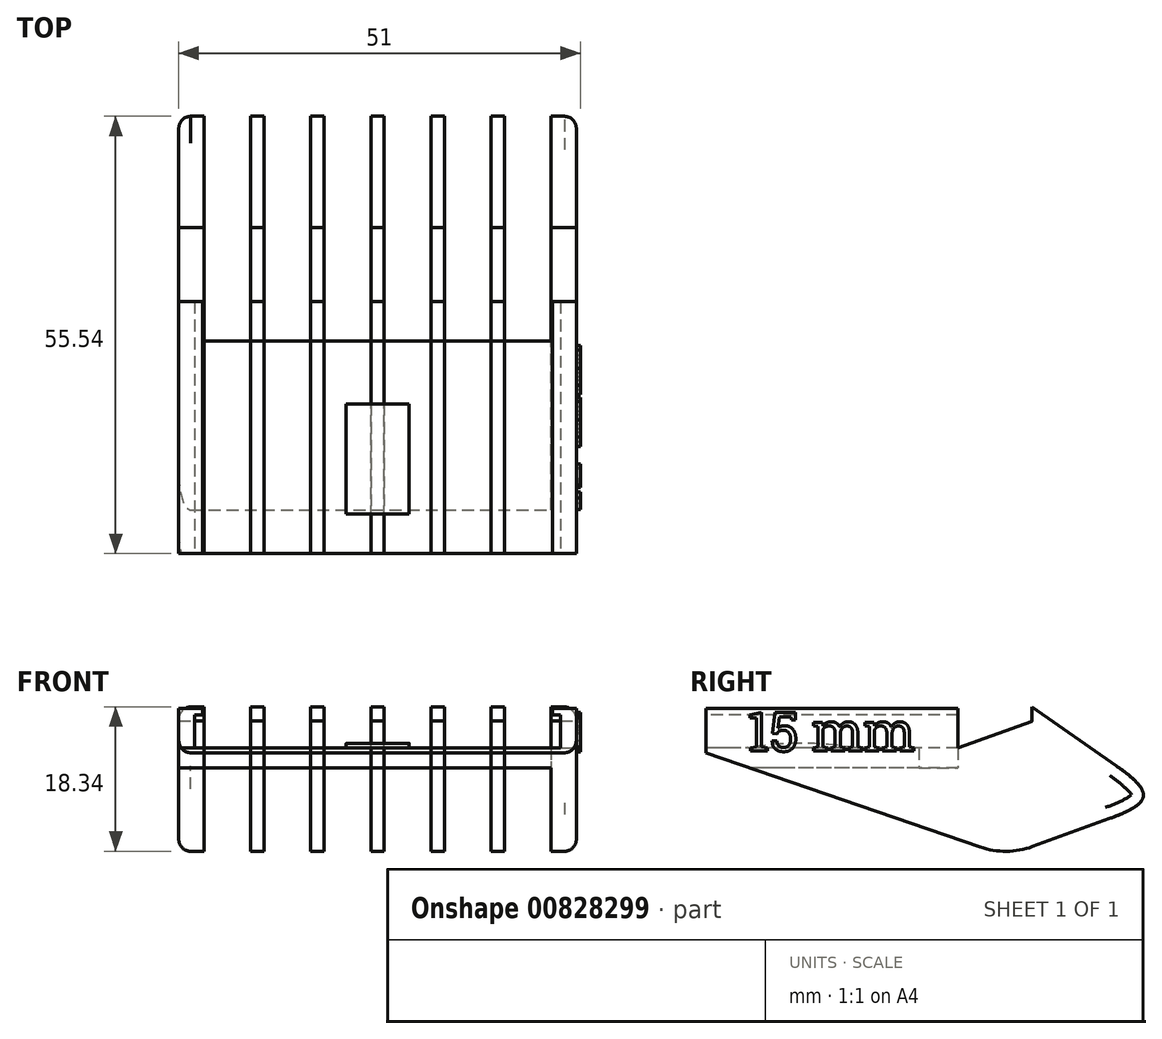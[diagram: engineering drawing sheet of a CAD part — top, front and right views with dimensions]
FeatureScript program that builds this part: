
annotation { "Feature Type Name" : "Feature", "Feature Type Description" : "" }
export const myFeature = defineFeature(function(context is Context, id is Id, definition is map)
    precondition{}
    {
        {
            var Q0;
            Q0=qCreatedBy(makeId("Top.planeOp"),FACE);
            var sketch = newSketch(context, id + "F0", { "sketchPlane" : qUnion([Q0])});
            skLineSegment(sketch, "E0.top", {"start": v(25.25, -16) * mm, "end": v(-25.25, -16) * mm});
            skLineSegment(sketch, "E0.left", {"start": v(25.25, 16) * mm, "end": v(25.25, -16) * mm});
            skLineSegment(sketch, "E0.right", {"start": v(-25.25, 16) * mm, "end": v(-25.25, -16) * mm});
            skPoint(sketch, "E0.middle", {"position": v(0, 0) * mm});
            skLineSegment(sketch, "E1", {"start": v(-22.05, 11) * mm, "end": v(22.05, 11) * mm});
            skLineSegment(sketch, "E2", {"start": v(22.05, 11) * mm, "end": v(22.05, 16) * mm});
            skLineSegment(sketch, "E3", {"start": v(22.05, 16) * mm, "end": v(25.25, 16) * mm});
            skLineSegment(sketch, "E4", {"start": v(-22.05, 11) * mm, "end": v(-22.05, 16) * mm});
            skLineSegment(sketch, "E5", {"start": v(-22.05, 16) * mm, "end": v(-25.25, 16) * mm});
            skSolve(sketch);
        }
        {
            var Q0;
            Q0=qSketchRegion(id+"F0",true);
            extrude(context, id + "F1", {"entities" : qUnion([Q0]), "depth" : 2.5 * mm, "offsetDistance" : 25 * mm});
        }
        {
            var Q0;
            Q0=makeQuery(id+"F1.opExtrude","SWEPT_FACE",FACE,{"disambiguationData":[OSD([sQuery(id+"F0.wireOp",EDGE,"E0.top")])]});
            var sketch = newSketch(context, id + "F2", { "sketchPlane" : qUnion([Q0])});
            skLineSegment(sketch, "E6.0", {"start": v(25.25, 2.5) * mm, "end": v(-25.25, 2.5) * mm});
            skLineSegment(sketch, "E7", {"start": v(25.25, 2.5) * mm, "end": v(25.25, 7.5) * mm});
            skLineSegment(sketch, "E8", {"start": v(25.25, 7.5) * mm, "end": v(22.25, 7.5) * mm});
            skLineSegment(sketch, "E9", {"start": v(22.25, 7.5) * mm, "end": v(22.25, 6.7) * mm});
            skLineSegment(sketch, "E10", {"start": v(22.25, 6.7) * mm, "end": v(23.25, 6.7) * mm});
            skLineSegment(sketch, "E11", {"start": v(23.25, 6.7) * mm, "end": v(23.25, 2.5) * mm});
            skLineSegment(sketch, "E12", {"start": v(23.25, 2.5) * mm, "end": v(25.25, 2.5) * mm});
            skLineSegment(sketch, "E13.MirrorCS", {"start": v(-25.25, 2.5) * mm, "end": v(-25.25, 7.5) * mm});
            skLineSegment(sketch, "E14.MirrorCS", {"start": v(-25.25, 7.5) * mm, "end": v(-22.25, 7.5) * mm});
            skLineSegment(sketch, "E15.MirrorCS", {"start": v(-22.25, 7.5) * mm, "end": v(-22.25, 6.7) * mm});
            skLineSegment(sketch, "E16.MirrorCS", {"start": v(-22.25, 6.7) * mm, "end": v(-23.25, 6.7) * mm});
            skLineSegment(sketch, "E17.MirrorCS", {"start": v(-23.25, 6.7) * mm, "end": v(-23.25, 2.5) * mm});
            skSolve(sketch);
        }
        {
            var Q0;
            Q0=qSketchRegion(id+"F2",true);
            var Q1;
            Q1=makeQuery(id+"F1.opExtrude","SWEPT_FACE",FACE,{"disambiguationData":[OSD([sQuery(id+"F0.wireOp",EDGE,"E3")])]});
            extrude(context, id + "F3", {"entities" : qUnion([Q0]), "operationType" : NewBodyOperationType.ADD, "endBound" : BoundingType.UP_TO_SURFACE, "oppositeDirection" : true, "depth" : 25 * mm, "endBoundEntityFace" : qUnion([Q1]), "offsetDistance" : 25 * mm});
        }
        {
            var Q0;
            Q0=makeQuery(id+"F3.boolean.opBoolean","MERGE",FACE,{"derivedFrom":[makeQuery(id+"F1.opExtrude","SWEPT_FACE",FACE,{"disambiguationData":[OSD([sQuery(id+"F0.wireOp",EDGE,"E0.left")])]}),makeQuery(id+"F3.opExtrude","SWEPT_FACE",FACE,{"disambiguationData":[OSD([sQuery(id+"F2.wireOp",EDGE,"E7")])]})]});
            var sketch = newSketch(context, id + "F4", { "sketchPlane" : qUnion([Q0])});
            skLineSegment(sketch, "E18.0", {"start": v(16, 2.5) * mm, "end": v(-16, 2.5) * mm});
            skLineSegment(sketch, "E19.0", {"start": v(11, 2.5) * mm, "end": v(11, 0) * mm});
            skLineSegment(sketch, "E20.0", {"start": v(16, 2.5) * mm, "end": v(16, 0) * mm});
            skLineSegment(sketch, "E21", {"start": v(11, 0) * mm, "end": v(11, 2.5) * mm});
            skLineSegment(sketch, "E22", {"start": v(11, 2.5) * mm, "end": v(16, 2.5) * mm});
            skLineSegment(sketch, "E23", {"start": v(16, 2.5) * mm, "end": v(25.4, 5.92) * mm});
            skLineSegment(sketch, "E24", {"start": v(25.4, 5.92) * mm, "end": v(25.4, 7.72) * mm});
            skLineSegment(sketch, "E25", {"start": v(25.4, 7.72) * mm, "end": v(42.09, -3.97) * mm});
            skLineSegment(sketch, "E26", {"start": v(42.09, -3.97) * mm, "end": v(25.46, -10.02) * mm});
            skArc(sketch, "E27", {"start": v(18.79, -10.08) * mm, "mid": v(22.13, -10.62) * mm, "end": v(25.46, -10.02) * mm});
            skLineSegment(sketch, "E28", {"start": v(-16, 1.9) * mm, "end": v(18.79, -10.08) * mm});
            skLineSegment(sketch, "E29", {"start": v(-16, 2.5) * mm, "end": v(-16, 1.9) * mm});
            skSolve(sketch);
        }
        {
            var Q0;
            Q0=qSketchRegion(id+"F4",true);
            var Q1;
            Q1=makeQuery(id+"F3.boolean.opBoolean","MERGE",FACE,{"derivedFrom":[makeQuery(id+"F1.opExtrude","SWEPT_FACE",FACE,{"disambiguationData":[OSD([sQuery(id+"F0.wireOp",EDGE,"E0.right")])]}),makeQuery(id+"F3.opExtrude","SWEPT_FACE",FACE,{"disambiguationData":[OSD([sQuery(id+"F2.wireOp",EDGE,"E13.MirrorCS")])]})]});
            extrude(context, id + "F5", {"entities" : qUnion([Q0]), "operationType" : NewBodyOperationType.ADD, "endBound" : BoundingType.UP_TO_SURFACE, "oppositeDirection" : true, "depth" : 25 * mm, "endBoundEntityFace" : qUnion([Q1]), "offsetDistance" : 25 * mm});
        }
        {
            var Q0;
            Q0=makeQuery(id+"F5.opExtrude","SWEPT_FACE",FACE,{"disambiguationData":[OSD([sQuery(id+"F4.wireOp",EDGE,"E26")])]});
            var sketch = newSketch(context, id + "F6", { "sketchPlane" : qUnion([Q0])});
            skLineSegment(sketch, "E30.bottom", {"start": v(22.05, -38.2) * mm, "end": v(16.12, -38.2) * mm});
            skLineSegment(sketch, "E30.top", {"start": v(22.05, 31.14) * mm, "end": v(16.12, 31.14) * mm});
            skLineSegment(sketch, "E30.left", {"start": v(22.05, -38.2) * mm, "end": v(22.05, 31.14) * mm});
            skLineSegment(sketch, "E30.right", {"start": v(16.12, -38.2) * mm, "end": v(16.12, 31.14) * mm});
            skLineSegment(sketch, "E31.1.0.0", {"start": v(14.42, -38.2) * mm, "end": v(14.42, 31.14) * mm});
            skLineSegment(sketch, "E31.1.0.1", {"start": v(8.48, -38.2) * mm, "end": v(8.48, 31.14) * mm});
            skLineSegment(sketch, "E31.1.0.2", {"start": v(14.42, 31.14) * mm, "end": v(8.48, 31.14) * mm});
            skLineSegment(sketch, "E31.1.0.3", {"start": v(14.42, -38.2) * mm, "end": v(8.48, -38.2) * mm});
            skLineSegment(sketch, "E31.2.0.0", {"start": v(6.78, -38.2) * mm, "end": v(6.78, 31.14) * mm});
            skLineSegment(sketch, "E31.2.0.1", {"start": v(0.85, -38.2) * mm, "end": v(0.85, 31.14) * mm});
            skLineSegment(sketch, "E31.2.0.2", {"start": v(6.78, 31.14) * mm, "end": v(0.85, 31.14) * mm});
            skLineSegment(sketch, "E31.2.0.3", {"start": v(6.78, -38.2) * mm, "end": v(0.85, -38.2) * mm});
            skLineSegment(sketch, "E31.3.0.0", {"start": v(-0.85, -38.2) * mm, "end": v(-0.85, 31.14) * mm});
            skLineSegment(sketch, "E31.3.0.1", {"start": v(-6.78, -38.2) * mm, "end": v(-6.78, 31.14) * mm});
            skLineSegment(sketch, "E31.3.0.2", {"start": v(-0.85, 31.14) * mm, "end": v(-6.78, 31.14) * mm});
            skLineSegment(sketch, "E31.3.0.3", {"start": v(-0.85, -38.2) * mm, "end": v(-6.78, -38.2) * mm});
            skLineSegment(sketch, "E31.4.0.0", {"start": v(-8.48, -38.2) * mm, "end": v(-8.48, 31.14) * mm});
            skLineSegment(sketch, "E31.4.0.1", {"start": v(-14.42, -38.2) * mm, "end": v(-14.42, 31.14) * mm});
            skLineSegment(sketch, "E31.4.0.2", {"start": v(-8.48, 31.14) * mm, "end": v(-14.42, 31.14) * mm});
            skLineSegment(sketch, "E31.4.0.3", {"start": v(-8.48, -38.2) * mm, "end": v(-14.42, -38.2) * mm});
            skLineSegment(sketch, "E31.5.0.0", {"start": v(-16.12, -38.2) * mm, "end": v(-16.12, 31.14) * mm});
            skLineSegment(sketch, "E31.5.0.1", {"start": v(-22.05, -38.2) * mm, "end": v(-22.05, 31.14) * mm});
            skLineSegment(sketch, "E31.5.0.2", {"start": v(-16.12, 31.14) * mm, "end": v(-22.05, 31.14) * mm});
            skLineSegment(sketch, "E31.5.0.3", {"start": v(-16.12, -38.2) * mm, "end": v(-22.05, -38.2) * mm});
            skLineSegment(sketch, "E31.direction1", {"start": v(22.05, -38.2) * mm, "end": v(14.42, -38.2) * mm, "construction": true});
            skSolve(sketch);
        }
        {
            var Q0;
            Q0=qSketchRegion(id+"F6",true);
            extrude(context, id + "F7", {"entities" : qUnion([Q0]), "operationType" : NewBodyOperationType.REMOVE, "endBound" : BoundingType.UP_TO_NEXT, "oppositeDirection" : true, "depth" : 25 * mm, "offsetDistance" : 25 * mm});
        }
        {
            var Q0;
            Q0=qSketchRegion(id+"F0",true);
            extrude(context, id + "F8", {"entities" : qUnion([Q0]), "depth" : 2.5 * mm, "offsetDistance" : 25 * mm});
        }
        {
            var Q0;
            Q0=qCreatedBy(makeId("Right.planeOp"),FACE);
            var sketch = newSketch(context, id + "F9", { "sketchPlane" : qUnion([Q0])});
            skLineSegment(sketch, "E32.0", {"start": v(16, 2.5) * mm, "end": v(-16, 2.5) * mm});
            skLineSegment(sketch, "E33.0", {"start": v(11, 2.5) * mm, "end": v(11, 0) * mm});
            skArc(sketch, "E34", {"start": v(3, 2.5) * mm, "mid": v(-4, 3.1) * mm, "end": v(-11, 2.5) * mm});
            skSolve(sketch);
        }
        {
            var Q0;
            Q0=qSketchRegion(id+"F9",true);
            extrude(context, id + "F10", {"entities" : qUnion([Q0]), "endBound" : BoundingType.SYMMETRIC, "depth" : 8 * mm, "offsetDistance" : 25 * mm});
        }
        {
            var Q0;
            {var subQ0=sQuery(id+"F4.wireOp",EDGE,"E25");var subQ1=sQuery(id+"F4.wireOp",EDGE,"E26");Q0=makeQuery(id+"F7.boolean.opBoolean","SPLIT",EDGE,{"disambiguationData":[TD([makeQuery(id+"F1.opExtrude","SWEPT_FACE",FACE,{"disambiguationData":[OSD([sQuery(id+"F0.wireOp",EDGE,"E0.right")])]})])],"derivedFrom":makeQuery(id+"F5.opExtrude","SWEPT_EDGE",EDGE,{"disambiguationData":[OSD([subQ0,subQ1])]})});}
            var Q1;
            {var subQ0=sQuery(id+"F4.wireOp",EDGE,"E25");var subQ1=sQuery(id+"F4.wireOp",EDGE,"E26");Q1=makeQuery(id+"F7.boolean.opBoolean","SPLIT",EDGE,{"disambiguationData":[TD([makeQuery(id+"F7.opExtrude","SWEPT_FACE",FACE,{"disambiguationData":[OSD([sQuery(id+"F6.wireOp",EDGE,"E31.8.0.1")])]})])],"derivedFrom":makeQuery(id+"F5.opExtrude","SWEPT_EDGE",EDGE,{"disambiguationData":[OSD([subQ0,subQ1])]})});}
            var Q2;
            {var subQ0=sQuery(id+"F4.wireOp",EDGE,"E25");var subQ1=sQuery(id+"F4.wireOp",EDGE,"E26");Q2=makeQuery(id+"F7.boolean.opBoolean","SPLIT",EDGE,{"disambiguationData":[TD([makeQuery(id+"F7.opExtrude","SWEPT_FACE",FACE,{"disambiguationData":[OSD([sQuery(id+"F6.wireOp",EDGE,"E31.7.0.1")])]})])],"derivedFrom":makeQuery(id+"F5.opExtrude","SWEPT_EDGE",EDGE,{"disambiguationData":[OSD([subQ0,subQ1])]})});}
            var Q3;
            {var subQ0=sQuery(id+"F4.wireOp",EDGE,"E25");var subQ1=sQuery(id+"F4.wireOp",EDGE,"E26");Q3=makeQuery(id+"F7.boolean.opBoolean","SPLIT",EDGE,{"disambiguationData":[TD([makeQuery(id+"F7.opExtrude","SWEPT_FACE",FACE,{"disambiguationData":[OSD([sQuery(id+"F6.wireOp",EDGE,"E31.6.0.1")])]})])],"derivedFrom":makeQuery(id+"F5.opExtrude","SWEPT_EDGE",EDGE,{"disambiguationData":[OSD([subQ0,subQ1])]})});}
            var Q4;
            {var subQ0=sQuery(id+"F4.wireOp",EDGE,"E25");var subQ1=sQuery(id+"F4.wireOp",EDGE,"E26");Q4=makeQuery(id+"F7.boolean.opBoolean","SPLIT",EDGE,{"disambiguationData":[TD([makeQuery(id+"F1.opExtrude","SWEPT_FACE",FACE,{"disambiguationData":[OSD([sQuery(id+"F0.wireOp",EDGE,"E0.right")])]})])],"derivedFrom":makeQuery(id+"F5.opExtrude","SWEPT_EDGE",EDGE,{"disambiguationData":[OSD([subQ0,subQ1])]})});}
            var Q5;
            {var subQ0=sQuery(id+"F4.wireOp",EDGE,"E25");var subQ1=sQuery(id+"F4.wireOp",EDGE,"E26");Q5=makeQuery(id+"F7.boolean.opBoolean","SPLIT",EDGE,{"disambiguationData":[TD([makeQuery(id+"F7.opExtrude","SWEPT_FACE",FACE,{"disambiguationData":[OSD([sQuery(id+"F6.wireOp",EDGE,"E31.4.0.1")])]})])],"derivedFrom":makeQuery(id+"F5.opExtrude","SWEPT_EDGE",EDGE,{"disambiguationData":[OSD([subQ0,subQ1])]})});}
            var Q6;
            {var subQ0=sQuery(id+"F4.wireOp",EDGE,"E25");var subQ1=sQuery(id+"F4.wireOp",EDGE,"E26");Q6=makeQuery(id+"F7.boolean.opBoolean","SPLIT",EDGE,{"disambiguationData":[TD([makeQuery(id+"F7.opExtrude","SWEPT_FACE",FACE,{"disambiguationData":[OSD([sQuery(id+"F6.wireOp",EDGE,"E31.3.0.1")])]})])],"derivedFrom":makeQuery(id+"F5.opExtrude","SWEPT_EDGE",EDGE,{"disambiguationData":[OSD([subQ0,subQ1])]})});}
            var Q7;
            {var subQ0=sQuery(id+"F4.wireOp",EDGE,"E25");var subQ1=sQuery(id+"F4.wireOp",EDGE,"E26");Q7=makeQuery(id+"F7.boolean.opBoolean","SPLIT",EDGE,{"disambiguationData":[TD([makeQuery(id+"F7.opExtrude","SWEPT_FACE",FACE,{"disambiguationData":[OSD([sQuery(id+"F6.wireOp",EDGE,"E31.2.0.1")])]})])],"derivedFrom":makeQuery(id+"F5.opExtrude","SWEPT_EDGE",EDGE,{"disambiguationData":[OSD([subQ0,subQ1])]})});}
            var Q8;
            {var subQ0=sQuery(id+"F4.wireOp",EDGE,"E25");var subQ1=sQuery(id+"F4.wireOp",EDGE,"E26");Q8=makeQuery(id+"F7.boolean.opBoolean","SPLIT",EDGE,{"disambiguationData":[TD([makeQuery(id+"F7.opExtrude","SWEPT_FACE",FACE,{"disambiguationData":[OSD([sQuery(id+"F6.wireOp",EDGE,"E31.1.0.1")])]})])],"derivedFrom":makeQuery(id+"F5.opExtrude","SWEPT_EDGE",EDGE,{"disambiguationData":[OSD([subQ0,subQ1])]})});}
            var Q9;
            {var subQ0=sQuery(id+"F4.wireOp",EDGE,"E25");var subQ1=sQuery(id+"F4.wireOp",EDGE,"E26");Q9=makeQuery(id+"F7.boolean.opBoolean","SPLIT",EDGE,{"disambiguationData":[TD([makeQuery(id+"F7.opExtrude","SWEPT_FACE",FACE,{"disambiguationData":[OSD([sQuery(id+"F6.wireOp",EDGE,"E30.right")])]})])],"derivedFrom":makeQuery(id+"F5.opExtrude","SWEPT_EDGE",EDGE,{"disambiguationData":[OSD([subQ0,subQ1])]})});}
            var Q10;
            {var subQ0=sQuery(id+"F4.wireOp",EDGE,"E25");var subQ1=sQuery(id+"F4.wireOp",EDGE,"E26");Q10=makeQuery(id+"F7.boolean.opBoolean","SPLIT",EDGE,{"disambiguationData":[TD([makeQuery(id+"F1.opExtrude","SWEPT_FACE",FACE,{"disambiguationData":[OSD([sQuery(id+"F0.wireOp",EDGE,"E0.left")])]})])],"derivedFrom":makeQuery(id+"F5.opExtrude","SWEPT_EDGE",EDGE,{"disambiguationData":[OSD([subQ0,subQ1])]})});}
            fillet(context, id + "F11", {"entities" : qUnion([Q0, Q1, Q2, Q3, Q4, Q5, Q6, Q7, Q8, Q9, Q10]), "radius" : 3.8 * mm, "tangentPropagation" : true, "rho" : 0.6, "crossSection" : FilletCrossSection.CONIC, "allowEdgeOverflow" : false});
        }
        {
            var Q0;
            Q0=makeQuery(id+"F5.boolean.opBoolean","MERGE",FACE,{"derivedFrom":[makeQuery(id+"F3.boolean.opBoolean","MERGE",FACE,{"derivedFrom":[makeQuery(id+"F1.opExtrude","SWEPT_FACE",FACE,{"disambiguationData":[OSD([sQuery(id+"F0.wireOp",EDGE,"E0.left")])]}),makeQuery(id+"F3.opExtrude","SWEPT_FACE",FACE,{"disambiguationData":[OSD([sQuery(id+"F2.wireOp",EDGE,"E7")])]})]}),makeQuery(id+"F5.opExtrude","CAP_FACE",FACE,{"disambiguationData":[OSD([sQuery(id+"F4.wireOp",EDGE,"E18.0"),sQuery(id+"F4.wireOp",EDGE,"E22"),sQuery(id+"F4.wireOp",EDGE,"E23"),sQuery(id+"F4.wireOp",EDGE,"E24"),sQuery(id+"F4.wireOp",EDGE,"E25"),sQuery(id+"F4.wireOp",EDGE,"E26"),sQuery(id+"F4.wireOp",EDGE,"E27"),sQuery(id+"F4.wireOp",EDGE,"E28"),sQuery(id+"F4.wireOp",EDGE,"E29")])],"isStart":true})]});
            var sketch = newSketch(context, id + "F12", { "sketchPlane" : qUnion([Q0])});
            skLineSegment(sketch, "E35.0", {"start": v(16, 0) * mm, "end": v(-16, 0) * mm});
            skText(sketch, "E36", { "text": "15 mm", "fontName": "RobotoSlab-Regular.ttf"});
            const initialGuessF12  = {"E36": [-0.01081, 0.0021, 1, 0, 0.005]};
            skSetInitialGuess(sketch, initialGuessF12);
            skSolve(sketch);
        }
        {
            var Q0;
            Q0=qSketchRegion(id+"F12",true);
            var Q1;
            Q1=qConstructionFilter(qBodyType(qCreatedBy(id+"F12",EDGE),BodyType.WIRE),ConstructionObject.NO);
            extrude(context, id + "F13", {"entities" : qUnion([Q0]), "operationType" : NewBodyOperationType.ADD, "surfaceEntities" : qUnion([Q1]), "depth" : 0.5 * mm, "offsetDistance" : 25 * mm});
        }
        {
            var Q0;
            Q0=makeQuery(id+"F5.boolean.opBoolean","MERGE",FACE,{"derivedFrom":[makeQuery(id+"F3.boolean.opBoolean","MERGE",FACE,{"derivedFrom":[makeQuery(id+"F1.opExtrude","SWEPT_FACE",FACE,{"disambiguationData":[OSD([sQuery(id+"F0.wireOp",EDGE,"E0.left")])]}),makeQuery(id+"F3.opExtrude","SWEPT_FACE",FACE,{"disambiguationData":[OSD([sQuery(id+"F2.wireOp",EDGE,"E7")])]})]}),makeQuery(id+"F5.opExtrude","CAP_FACE",FACE,{"disambiguationData":[OSD([sQuery(id+"F4.wireOp",EDGE,"E18.0"),sQuery(id+"F4.wireOp",EDGE,"E22"),sQuery(id+"F4.wireOp",EDGE,"E23"),sQuery(id+"F4.wireOp",EDGE,"E24"),sQuery(id+"F4.wireOp",EDGE,"E25"),sQuery(id+"F4.wireOp",EDGE,"E26"),sQuery(id+"F4.wireOp",EDGE,"E27"),sQuery(id+"F4.wireOp",EDGE,"E28"),sQuery(id+"F4.wireOp",EDGE,"E29")])],"isStart":true})]});
            var sketch = newSketch(context, id + "F14", { "sketchPlane" : qUnion([Q0])});
            skLineSegment(sketch, "E37", {"start": v(-16, 1.9) * mm, "end": v(-10.48, 0) * mm});
            skLineSegment(sketch, "E38", {"start": v(-16, 1.9) * mm, "end": v(-16, 0) * mm});
            skLineSegment(sketch, "E39", {"start": v(-16, 0) * mm, "end": v(-10.48, 0) * mm});
            skSolve(sketch);
        }
        {
            var Q0;
            Q0 = qSketchRegion(id + "F14", true);
            extrude(context, id + "F15", {"entities" : qUnion([Q0]), "operationType" : NewBodyOperationType.REMOVE, "endBound" : BoundingType.THROUGH_ALL, "oppositeDirection" : true, "depth" : 25 * mm, "offsetDistance" : 25 * mm});
        }
        {
            var Q0;
            Q0=makeQuery(id+"F5.opExtrude","CAP_EDGE",EDGE,{"disambiguationData":[OSD([sQuery(id+"F4.wireOp",EDGE,"E26")])],"isStart":true});
            var Q1;
            Q1=makeQuery(id+"F5.opExtrude","CAP_EDGE",EDGE,{"disambiguationData":[OSD([sQuery(id+"F4.wireOp",EDGE,"E26")])],"isStart":false});
            var Q2;
            Q2=makeQuery(id+"F15.boolean.opBoolean","COPY",EDGE,{"derivedFrom":makeQuery(id+"F15.opExtrude","CAP_EDGE",EDGE,{"disambiguationData":[OSD([sQuery(id+"F14.wireOp",EDGE,"E37")])],"isStart":true})});
            var Q3;
            Q3=makeQuery(id+"F15.boolean.opBoolean","MERGE",EDGE,{"derivedFrom":[makeQuery(id+"F5.opExtrude","CAP_EDGE",EDGE,{"disambiguationData":[OSD([sQuery(id+"F4.wireOp",EDGE,"E28")])],"isStart":true})],"fromTools":[makeQuery(id+"F15.opExtrude","CAP_EDGE",EDGE,{"disambiguationData":[OSD([sQuery(id+"F14.wireOp",EDGE,"E37")])],"isStart":true})]});
            var Q4;
            Q4=makeQuery(id+"F15.boolean.opBoolean","INTERSECT",EDGE,{"derivedFrom":[makeQuery(id+"F8.opExtrude","SWEPT_FACE",FACE,{"disambiguationData":[OSD([sQuery(id+"F0.wireOp",EDGE,"E0.right")])]}),makeQuery(id+"F15.opExtrude","SWEPT_FACE",FACE,{"disambiguationData":[OSD([sQuery(id+"F14.wireOp",EDGE,"E37")])]})]});
            var Q5;
            Q5=makeQuery(id+"F15.boolean.opBoolean","INTERSECT",EDGE,{"derivedFrom":[makeQuery(id+"F5.boolean.opBoolean","MERGE",FACE,{"derivedFrom":[makeQuery(id+"F3.boolean.opBoolean","MERGE",FACE,{"derivedFrom":[makeQuery(id+"F1.opExtrude","SWEPT_FACE",FACE,{"disambiguationData":[OSD([sQuery(id+"F0.wireOp",EDGE,"E0.right")])]}),makeQuery(id+"F3.opExtrude","SWEPT_FACE",FACE,{"disambiguationData":[OSD([sQuery(id+"F2.wireOp",EDGE,"E13.MirrorCS")])]})]}),makeQuery(id+"F5.opExtrude","CAP_FACE",FACE,{"disambiguationData":[OSD([sQuery(id+"F4.wireOp",EDGE,"E18.0"),sQuery(id+"F4.wireOp",EDGE,"E22"),sQuery(id+"F4.wireOp",EDGE,"E23"),sQuery(id+"F4.wireOp",EDGE,"E24"),sQuery(id+"F4.wireOp",EDGE,"E25"),sQuery(id+"F4.wireOp",EDGE,"E26"),sQuery(id+"F4.wireOp",EDGE,"E27"),sQuery(id+"F4.wireOp",EDGE,"E28"),sQuery(id+"F4.wireOp",EDGE,"E29")])],"isStart":false})]}),makeQuery(id+"F15.opExtrude","SWEPT_FACE",FACE,{"disambiguationData":[OSD([sQuery(id+"F14.wireOp",EDGE,"E37")])]})]});
            fillet(context, id + "F16", {"entities" : qUnion([Q0, Q1, Q2, Q3, Q4, Q5]), "radius" : 1.5 * mm, "tangentPropagation" : true, "allowEdgeOverflow" : false});
        }
    });
